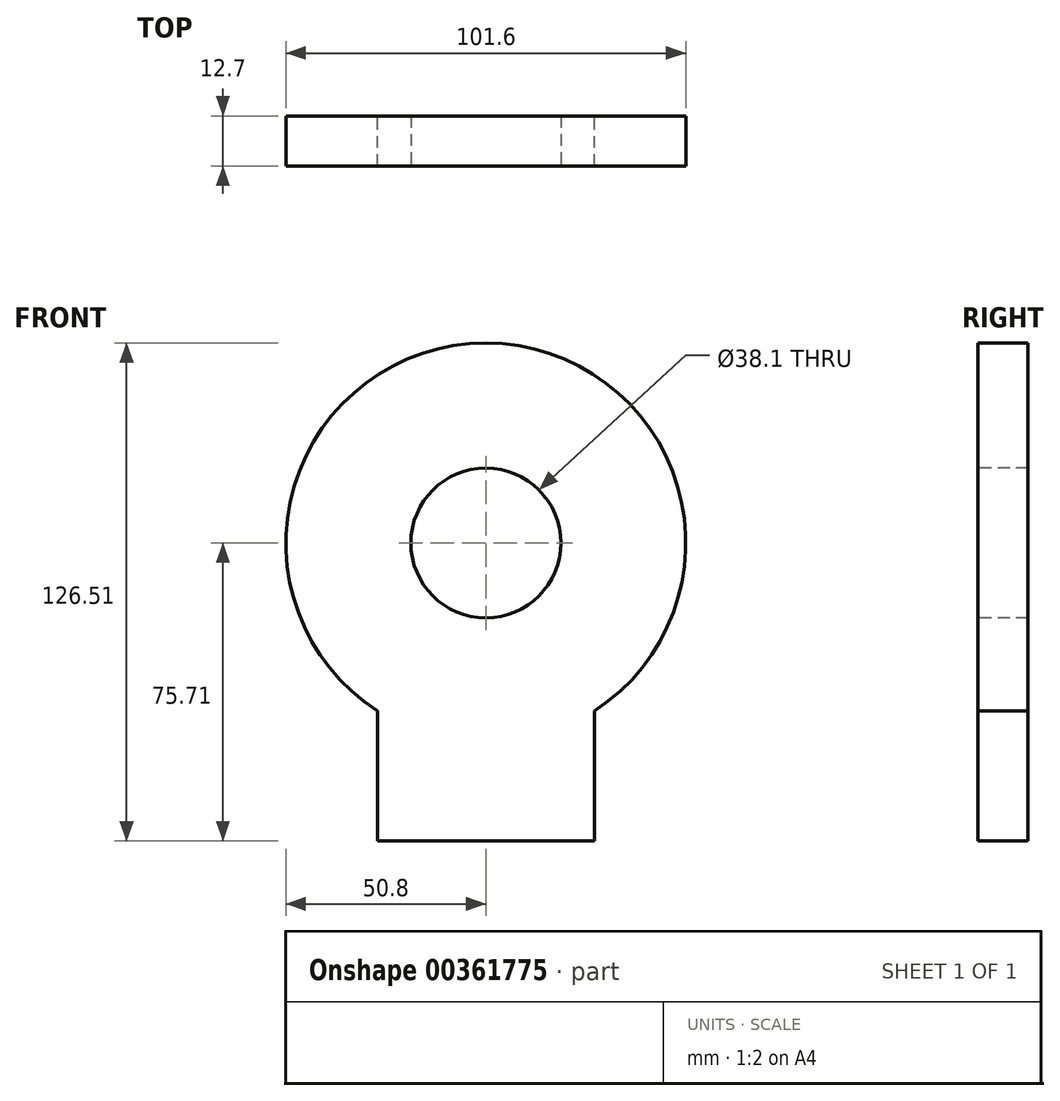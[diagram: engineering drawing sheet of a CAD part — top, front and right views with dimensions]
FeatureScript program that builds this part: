
annotation { "Feature Type Name" : "Feature", "Feature Type Description" : "" }
export const myFeature = defineFeature(function(context is Context, id is Id, definition is map)
    precondition{}
    {
        {
            var Q0;
            Q0=qCreatedBy(makeId("Front.planeOp"),FACE);
            var sketch = newSketch(context, id + "F0", { "sketchPlane" : qUnion([Q0])});
            skArc(sketch, "E0", {"start": v(27.53, -42.7) * mm, "mid": v(0, 50.8) * mm, "end": v(-27.53, -42.7) * mm});
            skLineSegment(sketch, "E1", {"start": v(27.53, -42.7) * mm, "end": v(27.53, -75.71) * mm});
            skLineSegment(sketch, "E2", {"start": v(27.53, -75.71) * mm, "end": v(-27.53, -75.71) * mm});
            skLineSegment(sketch, "E3", {"start": v(-27.53, -75.71) * mm, "end": v(-27.53, -42.7) * mm});
            skSolve(sketch);
        }
        {
            var Q0;
            Q0=makeQuery(id+"F0.imprint","IMPRINT",FACE,{"disambiguationData":[TD([[makeQuery(id+"F0.imprint","IMPRINT",EDGE,{"derivedFrom":sQuery(id+"F0.wireOp",EDGE,"E0")}),1.0]])]});
            extrude(context, id + "F1", {"entities" : qUnion([Q0]), "depth" : 12.7 * mm});
        }
        {
            var Q0;
            Q0=makeQuery(id+"F1.opExtrude","CAP_FACE",FACE,{"disambiguationData":[OSD([sQuery(id+"F0.wireOp",EDGE,"E0")])],"isStart":false});
            var sketch = newSketch(context, id + "F2", { "sketchPlane" : qUnion([Q0])});
            skCircle(sketch, "E4", {"center": v(0, 0) * mm, "radius": 19.05 * mm});
            skSolve(sketch);
        }
        {
            var Q0;
            Q0=sQuery(id+"F2.wireOp",VERTEX,"E4.center");
            var Q1;
            Q1=makeQuery(id+"F1.opExtrude","SWEPT_BODY",BODY,{"disambiguationData":[OSD([sQuery(id+"F0.wireOp",EDGE,"E0")])]});
            hole(context, id + "F3", {"style" : HoleStyle.SIMPLE, "endStyle" : HoleEndStyle.THROUGH, "holeDiameter" : 38.1 * mm, "isTappedThrough" : true, "tappedDepth" : 12.7 * mm, "tapClearance" : 3, "locations" : qUnion([Q0]), "scope" : qUnion([Q1])});
        }
    });
